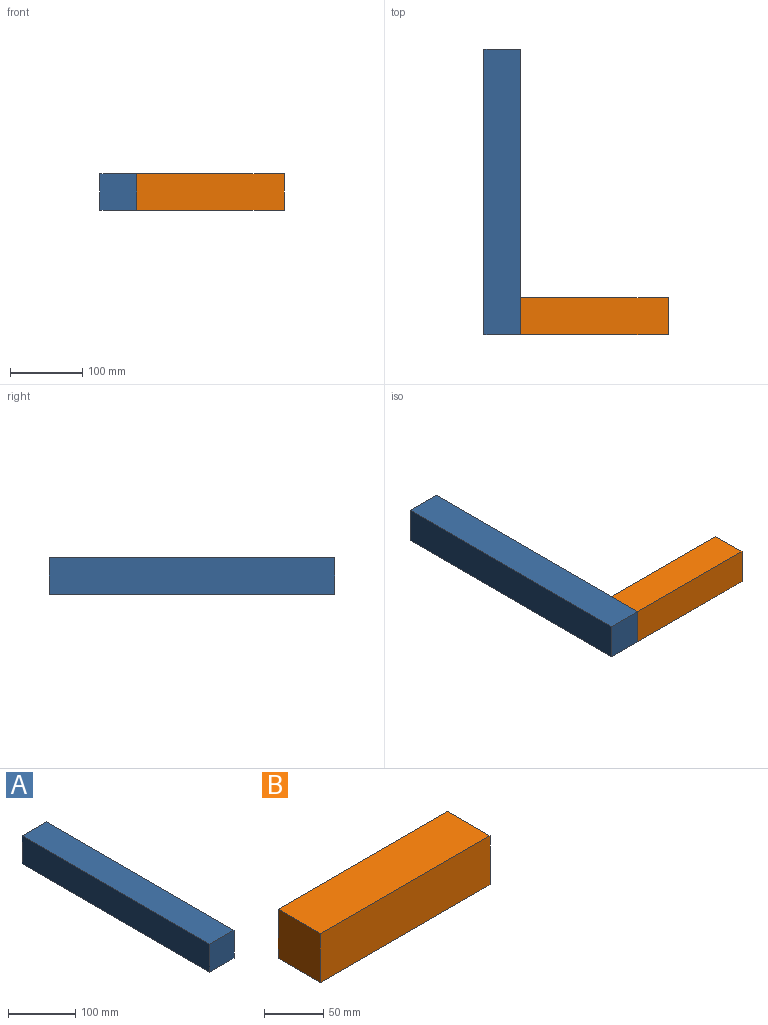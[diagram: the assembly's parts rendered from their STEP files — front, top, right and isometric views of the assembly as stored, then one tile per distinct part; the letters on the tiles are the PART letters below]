
ASSEMBLY  parts=2 mates=1
PART A: 6 faces, bbox 50.8x393.7x50.8 mm
  f0: plane 50.8x50.8mm, normal (0,-1,0), area 2580.6mm2, adj f1,f3,f4,f5
  f1: plane 393.7x50.8mm, normal (1,0,0), area 20000mm2, adj f0,f2,f4,f5
  f2: plane 50.8x50.8mm, normal (0,1,0), area 2580.6mm2, adj f1,f3,f4,f5
  f3: plane 393.7x50.8mm, normal (-1,0,0), area 20000mm2, adj f0,f2,f4,f5
  f4: plane 393.7x50.8mm, normal (0,0,1), area 20000mm2, adj f0,f1,f2,f3
  f5: plane 393.7x50.8mm, normal (0,0,-1), area 20000mm2, adj f0,f1,f2,f3
PART B: 6 faces, bbox 203.2x50.8x50.8 mm
  f0: plane 203.2x50.8mm, normal (0,-1,0), area 10322.6mm2, adj f1,f3,f4,f5
  f1: plane 50.8x50.8mm, normal (1,0,0), area 2580.6mm2, adj f0,f2,f4,f5
  f2: plane 203.2x50.8mm, normal (0,1,0), area 10322.6mm2, adj f1,f3,f4,f5
  f3: plane 50.8x50.8mm, normal (-1,0,0), area 2580.6mm2, adj f0,f2,f4,f5
  f4: plane 203.2x50.8mm, normal (0,0,1), area 10322.6mm2, adj f0,f1,f2,f3
  f5: plane 203.2x50.8mm, normal (0,0,-1), area 10322.6mm2, adj f0,f1,f2,f3
PLACE A t=(-27.4,41.97,11.39)mm
PLACE B t=(175.8,35.84,11.39)mm
MATE fastened A.f1 <-> B.f3  axis (1,0,0) through (-27.4,41.97,62.19)mm
